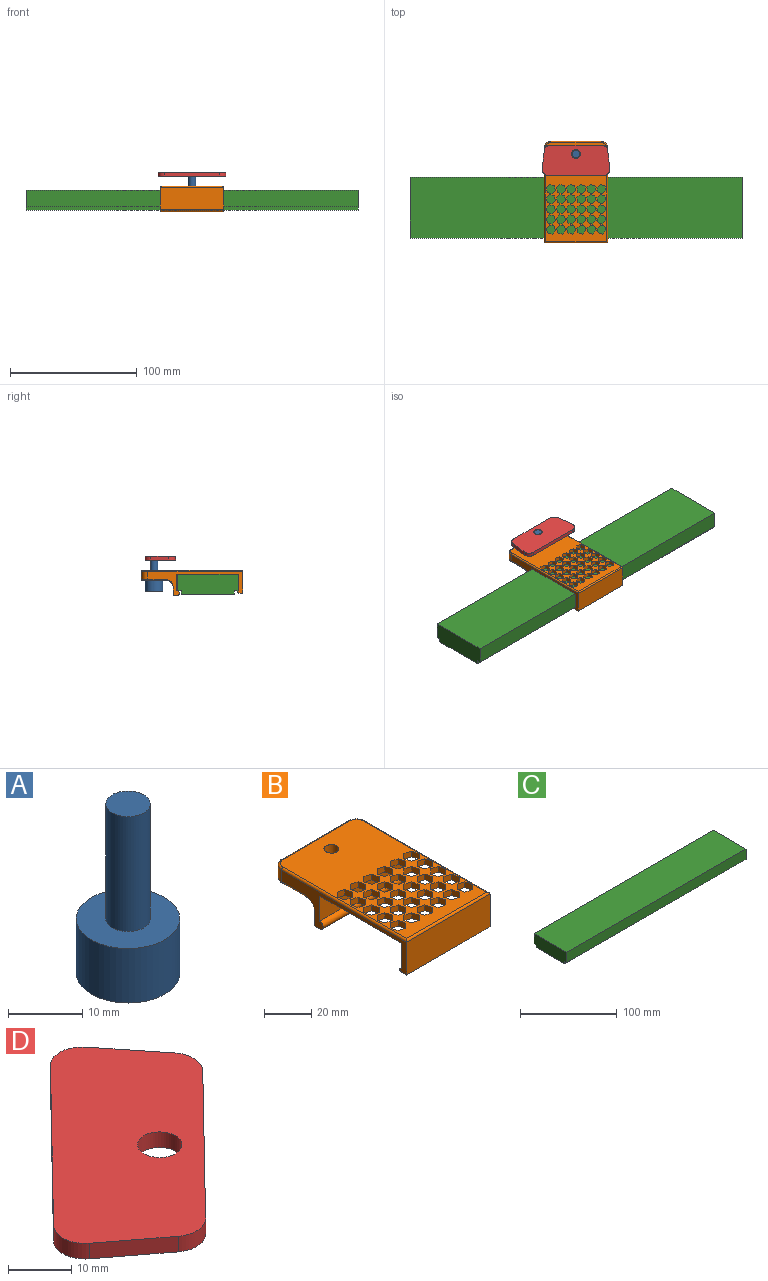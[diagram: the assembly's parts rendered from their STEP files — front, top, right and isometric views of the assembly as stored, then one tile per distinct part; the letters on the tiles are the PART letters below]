
ASSEMBLY  parts=4 mates=3
PART A: 5 faces, bbox 14x14x28 mm
  f0: cylinder r=3mm len=19mm, axis (0,0,-1), area 358.1mm2, adj f1,f3
  f1: plane 6x6mm, normal (0,0,1), area 28.3mm2, adj f0
  f2: cylinder r=7mm len=14mm, axis (0,0,-1), area 395.8mm2, adj f3,f4
  f3: plane 14x14mm, normal (0,0,1), area 125.7mm2, adj f0,f2
  f4: plane 14x14mm, normal (0,0,-1), area 153.9mm2, adj f2
PART B: 211 faces, bbox 68.7x80.4x20 mm
  f0: plane 78x48mm, normal (0,0,1), area 2607.8mm2, adj f14,f22,f23,f24,f25,f26,f27,f28
  f1: plane 50x49mm, normal (0,0,-1), area 1352.3mm2, adj f9,f10,f12,f13,f28,f29,f30,f31
  f2: plane 50x3mm, normal (0,0,-1), area 150mm2, adj f3,f11,f12,f13
  f3: plane 50x7.08mm, normal (0,1,0), area 350.1mm2, adj f2,f12,f13,f208,f209,f210
  f4: plane 48x19mm, normal (0,0,-1), area 873.5mm2, adj f14,f17,f18,f19,f20,f21,f209
  f5: plane 40x6mm, normal (0,1,0), area 240mm2, adj f15,f16,f19,f23
  f6: plane 50x17mm, normal (0,-1,0), area 850mm2, adj f7,f12,f13,f26
  f7: plane 50x3mm, normal (0,0,-1), area 150mm2, adj f6,f8,f12,f13
  f8: cylinder r=1mm len=50mm, axis (-1,0,0), area 159mm2, adj f7,f9,f12,f13
  f9: plane 50x13mm, normal (0,1,0), area 650mm2, adj f1,f8,f12,f13
  f10: plane 50x13mm, normal (0,-1,0), area 650mm2, adj f1,f11,f12,f13
  f11: cylinder r=2mm len=50mm, axis (-1,0,0), area 312.2mm2, adj f2,f10,f12,f13
  f12: plane 75x19mm, normal (1,0,0), area 342.2mm2, adj f1,f2,f3,f6,f7,f8,f9,f10
  f13: plane 75x19mm, normal (-1,0,0), area 342.2mm2, adj f1,f2,f3,f6,f7,f8,f9,f10
  f14: cylinder r=3.17mm len=8mm, axis (0,0,1), area 159.6mm2, adj f0,f4
  f15: cylinder r=5mm len=6mm, axis (0,0,1), area 47.1mm2, adj f5,f13,f20,f22
  f16: cylinder r=5mm len=6mm, axis (0,0,-1), area 47.1mm2, adj f5,f12,f18,f25
  f17: cylinder r=1mm len=15mm, axis (0,-1,0), area 23.6mm2, adj f4,f12,f18,f210
  f18: torus R=4mm, axis (0,0,1), area 11.4mm2, adj f4,f16,f17,f19
  f19: cylinder r=1mm len=40mm, axis (-1,0,0), area 62.8mm2, adj f4,f5,f18,f20
  f20: torus R=4mm, axis (0,0,1), area 11.4mm2, adj f4,f15,f19,f21
  f21: cylinder r=1mm len=15mm, axis (0,1,0), area 23.6mm2, adj f4,f13,f20,f208
  f22: torus R=4mm, axis (0,0,-1), area 11.4mm2, adj f0,f15,f23,f24
  f23: cylinder r=1mm len=40mm, axis (-1,0,0), area 62.8mm2, adj f0,f5,f22,f25
  f24: cylinder r=1mm len=75mm, axis (0,-1,0), area 117.2mm2, adj f0,f13,f22,f26
  f25: torus R=4mm, axis (0,0,-1), area 11.4mm2, adj f0,f16,f23,f27
  f26: cylinder r=1mm len=50mm, axis (-1,0,0), area 77.4mm2, adj f0,f6,f24,f27
  f27: cylinder r=1mm len=75mm, axis (0,1,0), area 117.2mm2, adj f0,f12,f25,f26
  f28: plane 3.61x3mm, normal (0.27,0.96,0), area 11.3mm2, adj f0,f1,f29,f31
  f29: plane 3.64x3mm, normal (0.97,0.25,0), area 11.3mm2, adj f0,f1,f28,f30
  f30: plane 3x2.69mm, normal (0.7,-0.72,0), area 11.3mm2, adj f0,f1,f29,f32
  f31: plane 3x2.69mm, normal (-0.7,0.72,0), area 11.3mm2, adj f0,f1,f28,f33
  f32: plane 3.61x3mm, normal (-0.27,-0.96,0), area 11.3mm2, adj f0,f1,f30,f33
  f33: plane 3.64x3mm, normal (-0.97,-0.25,0), area 11.3mm2, adj f0,f1,f31,f32
  f34: plane 3x2.69mm, normal (-0.7,0.72,0), area 11.3mm2, adj f0,f1,f35,f37
  f35: plane 3.61x3mm, normal (0.27,0.96,0), area 11.3mm2, adj f0,f1,f34,f36
  f36: plane 3.64x3mm, normal (0.97,0.25,0), area 11.3mm2, adj f0,f1,f35,f38
  f37: plane 3.64x3mm, normal (-0.97,-0.25,0), area 11.3mm2, adj f0,f1,f34,f39
  f38: plane 3x2.69mm, normal (0.7,-0.72,0), area 11.3mm2, adj f0,f1,f36,f39
  f39: plane 3.61x3mm, normal (-0.27,-0.96,0), area 11.3mm2, adj f0,f1,f37,f38
  f40: plane 3x2.69mm, normal (-0.7,0.72,0), area 11.3mm2, adj f0,f1,f41,f43
  f41: plane 3.61x3mm, normal (0.27,0.96,0), area 11.3mm2, adj f0,f1,f40,f42
  f42: plane 3.64x3mm, normal (0.97,0.25,0), area 11.3mm2, adj f0,f1,f41,f44
  f43: plane 3.64x3mm, normal (-0.97,-0.25,0), area 11.3mm2, adj f0,f1,f40,f45
  f44: plane 3x2.69mm, normal (0.7,-0.72,0), area 11.3mm2, adj f0,f1,f42,f45
  f45: plane 3.61x3mm, normal (-0.27,-0.96,0), area 11.3mm2, adj f0,f1,f43,f44
  f46: plane 3x2.69mm, normal (-0.7,0.72,0), area 11.3mm2, adj f0,f1,f47,f49
  f47: plane 3.61x3mm, normal (0.27,0.96,0), area 11.3mm2, adj f0,f1,f46,f48
  f48: plane 3.64x3mm, normal (0.97,0.25,0), area 11.3mm2, adj f0,f1,f47,f50
  f49: plane 3.64x3mm, normal (-0.97,-0.25,0), area 11.3mm2, adj f0,f1,f46,f51
  f50: plane 3x2.69mm, normal (0.7,-0.72,0), area 11.3mm2, adj f0,f1,f48,f51
  f51: plane 3.61x3mm, normal (-0.27,-0.96,0), area 11.3mm2, adj f0,f1,f49,f50
  f52: plane 3x2.69mm, normal (-0.7,0.72,0), area 11.3mm2, adj f0,f1,f53,f55
  f53: plane 3.61x3mm, normal (0.27,0.96,0), area 11.3mm2, adj f0,f1,f52,f54
  f54: plane 3.64x3mm, normal (0.97,0.25,0), area 11.3mm2, adj f0,f1,f53,f56
  f55: plane 3.64x3mm, normal (-0.97,-0.25,0), area 11.3mm2, adj f0,f1,f52,f57
  f56: plane 3x2.69mm, normal (0.7,-0.72,0), area 11.3mm2, adj f0,f1,f54,f57
  f57: plane 3.61x3mm, normal (-0.27,-0.96,0), area 11.3mm2, adj f0,f1,f55,f56
  f58: plane 3x2.69mm, normal (-0.7,0.72,0), area 11.3mm2, adj f0,f1,f59,f61
  f59: plane 3.61x3mm, normal (0.27,0.96,0), area 11.3mm2, adj f0,f1,f58,f60
  f60: plane 3.64x3mm, normal (0.97,0.25,0), area 11.3mm2, adj f0,f1,f59,f62
  f61: plane 3.64x3mm, normal (-0.97,-0.25,0), area 11.3mm2, adj f0,f1,f58,f63
  f62: plane 3x2.69mm, normal (0.7,-0.72,0), area 11.3mm2, adj f0,f1,f60,f63
  f63: plane 3.61x3mm, normal (-0.27,-0.96,0), area 11.3mm2, adj f0,f1,f61,f62
  f64: plane 3x2.69mm, normal (-0.7,0.72,0), area 11.3mm2, adj f0,f1,f65,f67
  f65: plane 3.61x3mm, normal (0.27,0.96,0), area 11.3mm2, adj f0,f1,f64,f66
  f66: plane 3.64x3mm, normal (0.97,0.25,0), area 11.3mm2, adj f0,f1,f65,f68
  f67: plane 3.64x3mm, normal (-0.97,-0.25,0), area 11.3mm2, adj f0,f1,f64,f69
  f68: plane 3x2.69mm, normal (0.7,-0.72,0), area 11.3mm2, adj f0,f1,f66,f69
  f69: plane 3.61x3mm, normal (-0.27,-0.96,0), area 11.3mm2, adj f0,f1,f67,f68
  f70: plane 3x2.69mm, normal (-0.7,0.72,0), area 11.3mm2, adj f0,f1,f71,f73
  f71: plane 3.61x3mm, normal (0.27,0.96,0), area 11.3mm2, adj f0,f1,f70,f72
  f72: plane 3.64x3mm, normal (0.97,0.25,0), area 11.3mm2, adj f0,f1,f71,f74
  f73: plane 3.64x3mm, normal (-0.97,-0.25,0), area 11.3mm2, adj f0,f1,f70,f75
  f74: plane 3x2.69mm, normal (0.7,-0.72,0), area 11.3mm2, adj f0,f1,f72,f75
  f75: plane 3.61x3mm, normal (-0.27,-0.96,0), area 11.3mm2, adj f0,f1,f73,f74
  f76: plane 3x2.69mm, normal (-0.7,0.72,0), area 11.3mm2, adj f0,f1,f77,f79
  f77: plane 3.61x3mm, normal (0.27,0.96,0), area 11.3mm2, adj f0,f1,f76,f78
  f78: plane 3.64x3mm, normal (0.97,0.25,0), area 11.3mm2, adj f0,f1,f77,f80
  f79: plane 3.64x3mm, normal (-0.97,-0.25,0), area 11.3mm2, adj f0,f1,f76,f81
  f80: plane 3x2.69mm, normal (0.7,-0.72,0), area 11.3mm2, adj f0,f1,f78,f81
  f81: plane 3.61x3mm, normal (-0.27,-0.96,0), area 11.3mm2, adj f0,f1,f79,f80
  f82: plane 3x2.69mm, normal (-0.7,0.72,0), area 11.3mm2, adj f0,f1,f83,f85
  f83: plane 3.61x3mm, normal (0.27,0.96,0), area 11.3mm2, adj f0,f1,f82,f84
  f84: plane 3.64x3mm, normal (0.97,0.25,0), area 11.3mm2, adj f0,f1,f83,f86
  f85: plane 3.64x3mm, normal (-0.97,-0.25,0), area 11.3mm2, adj f0,f1,f82,f87
  f86: plane 3x2.69mm, normal (0.7,-0.72,0), area 11.3mm2, adj f0,f1,f84,f87
  f87: plane 3.61x3mm, normal (-0.27,-0.96,0), area 11.3mm2, adj f0,f1,f85,f86
  f88: plane 3x2.69mm, normal (-0.7,0.72,0), area 11.3mm2, adj f0,f1,f89,f91
  f89: plane 3.61x3mm, normal (0.27,0.96,0), area 11.3mm2, adj f0,f1,f88,f90
  f90: plane 3.64x3mm, normal (0.97,0.25,0), area 11.3mm2, adj f0,f1,f89,f92
  f91: plane 3.64x3mm, normal (-0.97,-0.25,0), area 11.3mm2, adj f0,f1,f88,f93
  f92: plane 3x2.69mm, normal (0.7,-0.72,0), area 11.3mm2, adj f0,f1,f90,f93
  f93: plane 3.61x3mm, normal (-0.27,-0.96,0), area 11.3mm2, adj f0,f1,f91,f92
  f94: plane 3x2.69mm, normal (-0.7,0.72,0), area 11.3mm2, adj f0,f1,f95,f97
  f95: plane 3.61x3mm, normal (0.27,0.96,0), area 11.3mm2, adj f0,f1,f94,f96
  f96: plane 3.64x3mm, normal (0.97,0.25,0), area 11.3mm2, adj f0,f1,f95,f98
  f97: plane 3.64x3mm, normal (-0.97,-0.25,0), area 11.3mm2, adj f0,f1,f94,f99
  f98: plane 3x2.69mm, normal (0.7,-0.72,0), area 11.3mm2, adj f0,f1,f96,f99
  f99: plane 3.61x3mm, normal (-0.27,-0.96,0), area 11.3mm2, adj f0,f1,f97,f98
  f100: plane 3x2.69mm, normal (-0.7,0.72,0), area 11.3mm2, adj f0,f1,f101,f103
  f101: plane 3.61x3mm, normal (0.27,0.96,0), area 11.3mm2, adj f0,f1,f100,f102
  f102: plane 3.64x3mm, normal (0.97,0.25,0), area 11.3mm2, adj f0,f1,f101,f104
  f103: plane 3.64x3mm, normal (-0.97,-0.25,0), area 11.3mm2, adj f0,f1,f100,f105
  f104: plane 3x2.69mm, normal (0.7,-0.72,0), area 11.3mm2, adj f0,f1,f102,f105
  f105: plane 3.61x3mm, normal (-0.27,-0.96,0), area 11.3mm2, adj f0,f1,f103,f104
  f106: plane 3x2.69mm, normal (-0.7,0.72,0), area 11.3mm2, adj f0,f1,f107,f109
  f107: plane 3.61x3mm, normal (0.27,0.96,0), area 11.3mm2, adj f0,f1,f106,f108
  f108: plane 3.64x3mm, normal (0.97,0.25,0), area 11.3mm2, adj f0,f1,f107,f110
  f109: plane 3.64x3mm, normal (-0.97,-0.25,0), area 11.3mm2, adj f0,f1,f106,f111
  f110: plane 3x2.69mm, normal (0.7,-0.72,0), area 11.3mm2, adj f0,f1,f108,f111
  f111: plane 3.61x3mm, normal (-0.27,-0.96,0), area 11.3mm2, adj f0,f1,f109,f110
  f112: plane 3x2.69mm, normal (-0.7,0.72,0), area 11.3mm2, adj f0,f1,f113,f115
  f113: plane 3.61x3mm, normal (0.27,0.96,0), area 11.3mm2, adj f0,f1,f112,f114
  f114: plane 3.64x3mm, normal (0.97,0.25,0), area 11.3mm2, adj f0,f1,f113,f116
  f115: plane 3.64x3mm, normal (-0.97,-0.25,0), area 11.3mm2, adj f0,f1,f112,f117
  f116: plane 3x2.69mm, normal (0.7,-0.72,0), area 11.3mm2, adj f0,f1,f114,f117
  f117: plane 3.61x3mm, normal (-0.27,-0.96,0), area 11.3mm2, adj f0,f1,f115,f116
  f118: plane 3x2.69mm, normal (-0.7,0.72,0), area 11.3mm2, adj f0,f1,f119,f121
  f119: plane 3.61x3mm, normal (0.27,0.96,0), area 11.3mm2, adj f0,f1,f118,f120
  f120: plane 3.64x3mm, normal (0.97,0.25,0), area 11.3mm2, adj f0,f1,f119,f122
  f121: plane 3.64x3mm, normal (-0.97,-0.25,0), area 11.3mm2, adj f0,f1,f118,f123
  f122: plane 3x2.69mm, normal (0.7,-0.72,0), area 11.3mm2, adj f0,f1,f120,f123
  f123: plane 3.61x3mm, normal (-0.27,-0.96,0), area 11.3mm2, adj f0,f1,f121,f122
  f124: plane 3x2.69mm, normal (-0.7,0.72,0), area 11.3mm2, adj f0,f1,f125,f127
  f125: plane 3.61x3mm, normal (0.27,0.96,0), area 11.3mm2, adj f0,f1,f124,f126
  f126: plane 3.64x3mm, normal (0.97,0.25,0), area 11.3mm2, adj f0,f1,f125,f128
  f127: plane 3.64x3mm, normal (-0.97,-0.25,0), area 11.3mm2, adj f0,f1,f124,f129
  f128: plane 3x2.69mm, normal (0.7,-0.72,0), area 11.3mm2, adj f0,f1,f126,f129
  f129: plane 3.61x3mm, normal (-0.27,-0.96,0), area 11.3mm2, adj f0,f1,f127,f128
  f130: plane 3x2.69mm, normal (-0.7,0.72,0), area 11.3mm2, adj f0,f1,f131,f133
  f131: plane 3.61x3mm, normal (0.27,0.96,0), area 11.3mm2, adj f0,f1,f130,f132
  f132: plane 3.64x3mm, normal (0.97,0.25,0), area 11.3mm2, adj f0,f1,f131,f134
  f133: plane 3.64x3mm, normal (-0.97,-0.25,0), area 11.3mm2, adj f0,f1,f130,f135
  f134: plane 3x2.69mm, normal (0.7,-0.72,0), area 11.3mm2, adj f0,f1,f132,f135
  f135: plane 3.61x3mm, normal (-0.27,-0.96,0), area 11.3mm2, adj f0,f1,f133,f134
  f136: plane 3x2.69mm, normal (-0.7,0.72,0), area 11.3mm2, adj f0,f1,f137,f139
  f137: plane 3.61x3mm, normal (0.27,0.96,0), area 11.3mm2, adj f0,f1,f136,f138
  f138: plane 3.64x3mm, normal (0.97,0.25,0), area 11.3mm2, adj f0,f1,f137,f140
  f139: plane 3.64x3mm, normal (-0.97,-0.25,0), area 11.3mm2, adj f0,f1,f136,f141
  f140: plane 3x2.69mm, normal (0.7,-0.72,0), area 11.3mm2, adj f0,f1,f138,f141
  f141: plane 3.61x3mm, normal (-0.27,-0.96,0), area 11.3mm2, adj f0,f1,f139,f140
  f142: plane 3x2.69mm, normal (-0.7,0.72,0), area 11.3mm2, adj f0,f1,f143,f145
  f143: plane 3.61x3mm, normal (0.27,0.96,0), area 11.3mm2, adj f0,f1,f142,f144
  f144: plane 3.64x3mm, normal (0.97,0.25,0), area 11.3mm2, adj f0,f1,f143,f146
  f145: plane 3.64x3mm, normal (-0.97,-0.25,0), area 11.3mm2, adj f0,f1,f142,f147
  f146: plane 3x2.69mm, normal (0.7,-0.72,0), area 11.3mm2, adj f0,f1,f144,f147
  f147: plane 3.61x3mm, normal (-0.27,-0.96,0), area 11.3mm2, adj f0,f1,f145,f146
  f148: plane 3x2.69mm, normal (-0.7,0.72,0), area 11.3mm2, adj f0,f1,f149,f151
  f149: plane 3.61x3mm, normal (0.27,0.96,0), area 11.3mm2, adj f0,f1,f148,f150
  f150: plane 3.64x3mm, normal (0.97,0.25,0), area 11.3mm2, adj f0,f1,f149,f152
  f151: plane 3.64x3mm, normal (-0.97,-0.25,0), area 11.3mm2, adj f0,f1,f148,f153
  f152: plane 3x2.69mm, normal (0.7,-0.72,0), area 11.3mm2, adj f0,f1,f150,f153
  f153: plane 3.61x3mm, normal (-0.27,-0.96,0), area 11.3mm2, adj f0,f1,f151,f152
  f154: plane 3x2.69mm, normal (-0.7,0.72,0), area 11.3mm2, adj f0,f1,f155,f157
  f155: plane 3.61x3mm, normal (0.27,0.96,0), area 11.3mm2, adj f0,f1,f154,f156
  f156: plane 3.64x3mm, normal (0.97,0.25,0), area 11.3mm2, adj f0,f1,f155,f158
  f157: plane 3.64x3mm, normal (-0.97,-0.25,0), area 11.3mm2, adj f0,f1,f154,f159
  f158: plane 3x2.69mm, normal (0.7,-0.72,0), area 11.3mm2, adj f0,f1,f156,f159
  f159: plane 3.61x3mm, normal (-0.27,-0.96,0), area 11.3mm2, adj f0,f1,f157,f158
  f160: plane 3x2.69mm, normal (-0.7,0.72,0), area 11.3mm2, adj f0,f1,f161,f163
  f161: plane 3.61x3mm, normal (0.27,0.96,0), area 11.3mm2, adj f0,f1,f160,f162
  f162: plane 3.64x3mm, normal (0.97,0.25,0), area 11.3mm2, adj f0,f1,f161,f164
  f163: plane 3.64x3mm, normal (-0.97,-0.25,0), area 11.3mm2, adj f0,f1,f160,f165
  f164: plane 3x2.69mm, normal (0.7,-0.72,0), area 11.3mm2, adj f0,f1,f162,f165
  f165: plane 3.61x3mm, normal (-0.27,-0.96,0), area 11.3mm2, adj f0,f1,f163,f164
  f166: plane 3x2.69mm, normal (-0.7,0.72,0), area 11.3mm2, adj f0,f1,f167,f169
  f167: plane 3.61x3mm, normal (0.27,0.96,0), area 11.3mm2, adj f0,f1,f166,f168
  f168: plane 3.64x3mm, normal (0.97,0.25,0), area 11.3mm2, adj f0,f1,f167,f170
  f169: plane 3.64x3mm, normal (-0.97,-0.25,0), area 11.3mm2, adj f0,f1,f166,f171
  f170: plane 3x2.69mm, normal (0.7,-0.72,0), area 11.3mm2, adj f0,f1,f168,f171
  f171: plane 3.61x3mm, normal (-0.27,-0.96,0), area 11.3mm2, adj f0,f1,f169,f170
  f172: plane 3x2.69mm, normal (-0.7,0.72,0), area 11.3mm2, adj f0,f1,f173,f175
  f173: plane 3.61x3mm, normal (0.27,0.96,0), area 11.3mm2, adj f0,f1,f172,f174
  f174: plane 3.64x3mm, normal (0.97,0.25,0), area 11.3mm2, adj f0,f1,f173,f176
  f175: plane 3.64x3mm, normal (-0.97,-0.25,0), area 11.3mm2, adj f0,f1,f172,f177
  f176: plane 3x2.69mm, normal (0.7,-0.72,0), area 11.3mm2, adj f0,f1,f174,f177
  f177: plane 3.61x3mm, normal (-0.27,-0.96,0), area 11.3mm2, adj f0,f1,f175,f176
  f178: plane 3x2.69mm, normal (-0.7,0.72,0), area 11.3mm2, adj f0,f1,f179,f181
  f179: plane 3.61x3mm, normal (0.27,0.96,0), area 11.3mm2, adj f0,f1,f178,f180
  f180: plane 3.64x3mm, normal (0.97,0.25,0), area 11.3mm2, adj f0,f1,f179,f182
  f181: plane 3.64x3mm, normal (-0.97,-0.25,0), area 11.3mm2, adj f0,f1,f178,f183
  f182: plane 3x2.69mm, normal (0.7,-0.72,0), area 11.3mm2, adj f0,f1,f180,f183
  f183: plane 3.61x3mm, normal (-0.27,-0.96,0), area 11.3mm2, adj f0,f1,f181,f182
  f184: plane 3x2.69mm, normal (-0.7,0.72,0), area 11.3mm2, adj f0,f1,f185,f187
  f185: plane 3.61x3mm, normal (0.27,0.96,0), area 11.3mm2, adj f0,f1,f184,f186
  f186: plane 3.64x3mm, normal (0.97,0.25,0), area 11.3mm2, adj f0,f1,f185,f188
  f187: plane 3.64x3mm, normal (-0.97,-0.25,0), area 11.3mm2, adj f0,f1,f184,f189
  f188: plane 3x2.69mm, normal (0.7,-0.72,0), area 11.3mm2, adj f0,f1,f186,f189
  f189: plane 3.61x3mm, normal (-0.27,-0.96,0), area 11.3mm2, adj f0,f1,f187,f188
  f190: plane 3x2.69mm, normal (-0.7,0.72,0), area 11.3mm2, adj f0,f1,f191,f193
  f191: plane 3.61x3mm, normal (0.27,0.96,0), area 11.3mm2, adj f0,f1,f190,f192
  f192: plane 3.64x3mm, normal (0.97,0.25,0), area 11.3mm2, adj f0,f1,f191,f194
  f193: plane 3.64x3mm, normal (-0.97,-0.25,0), area 11.3mm2, adj f0,f1,f190,f195
  f194: plane 3x2.69mm, normal (0.7,-0.72,0), area 11.3mm2, adj f0,f1,f192,f195
  f195: plane 3.61x3mm, normal (-0.27,-0.96,0), area 11.3mm2, adj f0,f1,f193,f194
  f196: plane 3x2.69mm, normal (-0.7,0.72,0), area 11.3mm2, adj f0,f1,f197,f199
  f197: plane 3.61x3mm, normal (0.27,0.96,0), area 11.3mm2, adj f0,f1,f196,f198
  f198: plane 3.64x3mm, normal (0.97,0.25,0), area 11.3mm2, adj f0,f1,f197,f200
  f199: plane 3.64x3mm, normal (-0.97,-0.25,0), area 11.3mm2, adj f0,f1,f196,f201
  f200: plane 3x2.69mm, normal (0.7,-0.72,0), area 11.3mm2, adj f0,f1,f198,f201
  f201: plane 3.61x3mm, normal (-0.27,-0.96,0), area 11.3mm2, adj f0,f1,f199,f200
  f202: plane 3x2.69mm, normal (-0.7,0.72,0), area 11.3mm2, adj f0,f1,f203,f205
  f203: plane 3.61x3mm, normal (0.27,0.96,0), area 11.3mm2, adj f0,f1,f202,f204
  f204: plane 3.64x3mm, normal (0.97,0.25,0), area 11.3mm2, adj f0,f1,f203,f206
  f205: plane 3.64x3mm, normal (-0.97,-0.25,0), area 11.3mm2, adj f0,f1,f202,f207
  f206: plane 3x2.69mm, normal (0.7,-0.72,0), area 11.3mm2, adj f0,f1,f204,f207
  f207: plane 3.61x3mm, normal (-0.27,-0.96,0), area 11.3mm2, adj f0,f1,f205,f206
  f208: torus R=6mm, axis (0,-1,0), area 8.6mm2, adj f3,f13,f21,f209
  f209: cylinder r=5mm len=48mm, axis (1,0,0), area 377mm2, adj f3,f4,f208,f210
  f210: torus R=6mm, axis (0,-1,0), area 8.6mm2, adj f3,f12,f17,f209
PART C: 10 faces, bbox 262.4x48x16 mm
  f0: plane 262.45x13mm, normal (0,-1,0), area 3411.8mm2, adj f3,f4,f5,f8
  f1: plane 262.45x13mm, normal (0,1,0), area 3411.8mm2, adj f3,f4,f5,f7
  f2: plane 262.45x42mm, normal (0,0,-1), area 11022.7mm2, adj f3,f4,f6,f9
  f3: plane 48x16mm, normal (-1,0,0), area 750mm2, adj f0,f1,f2,f5,f6,f7,f8,f9
  f4: plane 48x16mm, normal (1,0,0), area 750mm2, adj f0,f1,f2,f5,f6,f7,f8,f9
  f5: plane 262.45x48mm, normal (0,0,1), area 12597.4mm2, adj f0,f1,f3,f4
  f6: plane 262.45x3mm, normal (0,1,0), area 787.3mm2, adj f2,f3,f4,f7
  f7: plane 262.45x3mm, normal (0,0,-1), area 787.3mm2, adj f1,f3,f4,f6
  f8: plane 262.45x3mm, normal (0,0,-1), area 787.3mm2, adj f0,f3,f4,f9
  f9: plane 262.45x3mm, normal (0,-1,0), area 787.3mm2, adj f2,f3,f4,f8
PART D: 11 faces, bbox 49.3x49.8x3 mm
  f0: plane 28.72x28.09mm, normal (0.71,-0.7,0), area 120.5mm2, adj f5,f6,f7,f10
  f1: plane 11.04x8.79mm, normal (0.78,0.62,0), area 42.3mm2, adj f5,f6,f7,f8
  f2: plane 31.22x30.54mm, normal (-0.71,0.7,0), area 131mm2, adj f5,f6,f8,f9
  f3: cylinder r=3.5mm len=7mm, axis (0,0,-1), area 66mm2, adj f5,f6
  f4: plane 11.23x8.54mm, normal (-0.61,-0.8,0), area 42.3mm2, adj f5,f6,f9,f10
  f5: plane 49.76x49.32mm, normal (0,0,1), area 1187.3mm2, adj f0,f1,f2,f3,f4,f7,f8,f9
  f6: plane 49.76x49.32mm, normal (0,0,-1), area 1187.3mm2, adj f0,f1,f2,f3,f4,f7,f8,f9
  f7: cylinder r=5mm len=6.61mm, axis (0,0,-1), area 21.7mm2, adj f0,f1,f5,f6
  f8: cylinder r=5mm len=7.49mm, axis (0,0,1), area 25.4mm2, adj f1,f2,f5,f6
  f9: cylinder r=5mm len=7.48mm, axis (0,0,-1), area 25.4mm2, adj f2,f4,f5,f6
  f10: cylinder r=5mm len=6.6mm, axis (0,0,1), area 21.7mm2, adj f0,f4,f5,f6
PLACE A t=(-174.83,-42,-89.9)mm
PLACE B t=(0,-7.5,0)mm
PLACE C t=(29.69,-104.4,-75.9)mm
PLACE D rot(axis=(0,0,1),134.4deg) t=(-151.01,-59.75,-64.9)mm
MATE fastened C.f5 <-> B.f1  axis (0,0,1) through (25,-97.7,-75.9)mm
MATE fastened A.f0 <-> B.f14  axis (0,0,1) through (25,-55.16,-80.9)mm
MATE revolute D.f3 <-> A.f0  axis (0,0,1) through (25,-55.16,-61.9)mm
